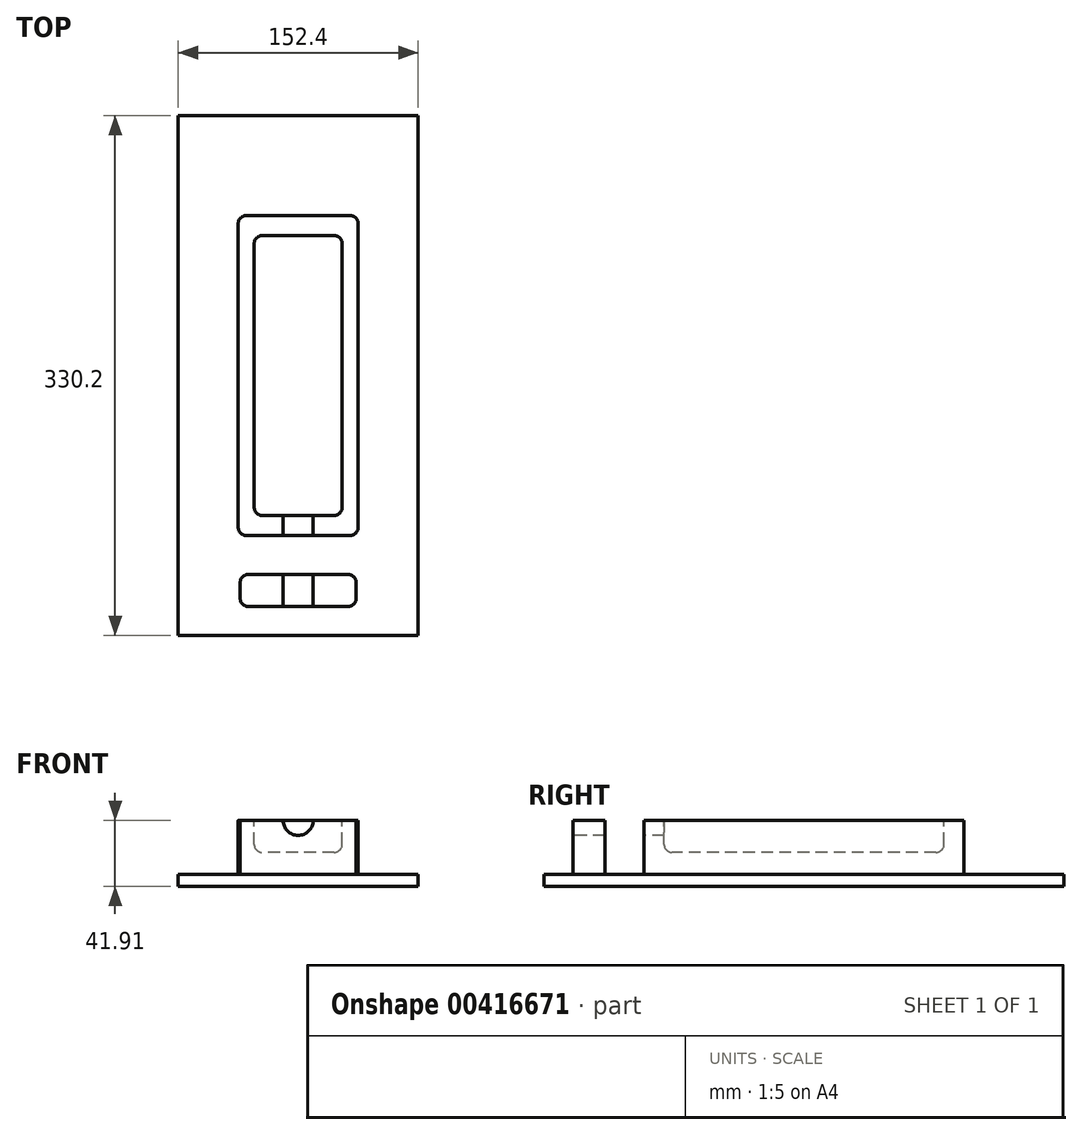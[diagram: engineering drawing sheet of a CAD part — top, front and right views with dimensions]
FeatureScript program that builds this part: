
annotation { "Feature Type Name" : "Feature", "Feature Type Description" : "" }
export const myFeature = defineFeature(function(context is Context, id is Id, definition is map)
    precondition{}
    {
        {
            var Q0;
            Q0=qCreatedBy(makeId("Top.planeOp"),FACE);
            var sketch = newSketch(context, id + "F0", { "sketchPlane" : qUnion([Q0])});
            skLineSegment(sketch, "E0.bottom", {"start": v(38.1, 101.6) * mm, "end": v(-38.1, 101.6) * mm});
            skLineSegment(sketch, "E0.top", {"start": v(38.1, -101.6) * mm, "end": v(-38.1, -101.6) * mm});
            skLineSegment(sketch, "E0.left", {"start": v(38.1, 101.6) * mm, "end": v(38.1, -101.6) * mm});
            skLineSegment(sketch, "E0.right", {"start": v(-38.1, 101.6) * mm, "end": v(-38.1, -101.6) * mm});
            skPoint(sketch, "E0.middle", {"position": v(0, 0) * mm});
            skSolve(sketch);
        }
        {
            var Q0;
            Q0=makeQuery(id+"F0.imprint","IMPRINT",FACE,{"disambiguationData":[TD([[makeQuery(id+"F0.imprint","IMPRINT",EDGE,{"derivedFrom":sQuery(id+"F0.wireOp",EDGE,"E0.bottom")}),1.0]])]});
            extrude(context, id + "F1", {"entities" : qUnion([Q0]), "endBound" : BoundingType.SYMMETRIC, "depth" : 38.1 * mm});
        }
        {
            var Q0;
            Q0=makeQuery(id+"F1.opExtrude","CAP_FACE",FACE,{"disambiguationData":[OSD([sQuery(id+"F0.wireOp",EDGE,"E0.bottom"),sQuery(id+"F0.wireOp",EDGE,"E0.top"),sQuery(id+"F0.wireOp",EDGE,"E0.left"),sQuery(id+"F0.wireOp",EDGE,"E0.right")])],"isStart":false});
            var sketch = newSketch(context, id + "F2", { "sketchPlane" : qUnion([Q0])});
            skLineSegment(sketch, "E1.bottom", {"start": v(27.94, 88.9) * mm, "end": v(-27.94, 88.9) * mm});
            skLineSegment(sketch, "E1.top", {"start": v(27.94, -88.9) * mm, "end": v(-27.94, -88.9) * mm});
            skLineSegment(sketch, "E1.left", {"start": v(27.94, 88.9) * mm, "end": v(27.94, -88.9) * mm});
            skLineSegment(sketch, "E1.right", {"start": v(-27.94, 88.9) * mm, "end": v(-27.94, -88.9) * mm});
            skPoint(sketch, "E1.middle", {"position": v(0, 0) * mm});
            skSolve(sketch);
        }
        {
            var Q0;
            Q0=makeQuery(id+"F2.imprint","IMPRINT",FACE,{"disambiguationData":[TD([[makeQuery(id+"F2.imprint","IMPRINT",EDGE,{"derivedFrom":sQuery(id+"F2.wireOp",EDGE,"E1.bottom")}),1.0]])]});
            extrude(context, id + "F3", {"entities" : qUnion([Q0]), "operationType" : NewBodyOperationType.REMOVE, "oppositeDirection" : true, "depth" : 20.32 * mm});
        }
        {
            var Q0;
            Q0=makeQuery(id+"F3.boolean.opBoolean","COPY",EDGE,{"derivedFrom":makeQuery(id+"F3.opExtrude","CAP_EDGE",EDGE,{"disambiguationData":[OSD([sQuery(id+"F2.wireOp",EDGE,"E1.right")])],"isStart":false})});
            var Q1;
            Q1=makeQuery(id+"F3.boolean.opBoolean","COPY",EDGE,{"derivedFrom":makeQuery(id+"F3.opExtrude","CAP_EDGE",EDGE,{"disambiguationData":[OSD([sQuery(id+"F2.wireOp",EDGE,"E1.bottom")])],"isStart":false})});
            var Q2;
            Q2=makeQuery(id+"F3.boolean.opBoolean","COPY",EDGE,{"derivedFrom":makeQuery(id+"F3.opExtrude","CAP_EDGE",EDGE,{"disambiguationData":[OSD([sQuery(id+"F2.wireOp",EDGE,"E1.left")])],"isStart":false})});
            var Q3;
            Q3=makeQuery(id+"F3.boolean.opBoolean","COPY",EDGE,{"derivedFrom":makeQuery(id+"F3.opExtrude","CAP_EDGE",EDGE,{"disambiguationData":[OSD([sQuery(id+"F2.wireOp",EDGE,"E1.top")])],"isStart":false})});
            var Q4;
            Q4=makeQuery(id+"F3.boolean.opBoolean","COPY",EDGE,{"derivedFrom":makeQuery(id+"F3.opExtrude","SWEPT_EDGE",EDGE,{"disambiguationData":[OSD([sQuery(id+"F2.wireOp",EDGE,"E1.bottom"),sQuery(id+"F2.wireOp",EDGE,"E1.right")])]})});
            var Q5;
            Q5=makeQuery(id+"F3.boolean.opBoolean","COPY",EDGE,{"derivedFrom":makeQuery(id+"F3.opExtrude","SWEPT_EDGE",EDGE,{"disambiguationData":[OSD([sQuery(id+"F2.wireOp",EDGE,"E1.bottom"),sQuery(id+"F2.wireOp",EDGE,"E1.left")])]})});
            var Q6;
            Q6=makeQuery(id+"F3.boolean.opBoolean","COPY",EDGE,{"derivedFrom":makeQuery(id+"F3.opExtrude","SWEPT_EDGE",EDGE,{"disambiguationData":[OSD([sQuery(id+"F2.wireOp",EDGE,"E1.top"),sQuery(id+"F2.wireOp",EDGE,"E1.left")])]})});
            var Q7;
            Q7=makeQuery(id+"F3.boolean.opBoolean","COPY",EDGE,{"derivedFrom":makeQuery(id+"F3.opExtrude","SWEPT_EDGE",EDGE,{"disambiguationData":[OSD([sQuery(id+"F2.wireOp",EDGE,"E1.top"),sQuery(id+"F2.wireOp",EDGE,"E1.right")])]})});
            var Q8;
            Q8=makeQuery(id+"F3.boolean.opBoolean","COPY",EDGE,{"derivedFrom":makeQuery(id+"F3.opExtrude","CAP_EDGE",EDGE,{"disambiguationData":[OSD([sQuery(id+"F2.wireOp",EDGE,"E1.bottom")])],"isStart":true})});
            fillet(context, id + "F4", {"entities" : qUnion([Q0, Q1, Q2, Q3, Q4, Q5, Q6, Q7, Q8]), "radius" : 5.08 * mm, "tangentPropagation" : true, "allowEdgeOverflow" : false});
        }
        {
            var Q0;
            Q0=makeQuery(id+"F1.opExtrude","SWEPT_FACE",FACE,{"disambiguationData":[OSD([sQuery(id+"F0.wireOp",EDGE,"E0.top")])]});
            var sketch = newSketch(context, id + "F5", { "sketchPlane" : qUnion([Q0])});
            skArc(sketch, "E2", {"start": v(-9.53, 19.05) * mm, "mid": v(0, 9.53) * mm, "end": v(9.52, 19.05) * mm});
            skSolve(sketch);
        }
        {
            var Q0;
            {var subQ0=sQuery(id+"F5.wireOp",EDGE,"E2");Q0=makeQuery(id+"F5.imprint","IMPRINT",FACE,{"disambiguationData":[TD([[makeQuery(id+"F5.imprint","IMPRINT",EDGE,{"derivedFrom":subQ0}),1.0]])]});}
            extrude(context, id + "F6", {"entities" : qUnion([Q0]), "operationType" : NewBodyOperationType.REMOVE, "oppositeDirection" : true, "depth" : 25.4 * mm});
        }
        {
            var Q0;
            Q0=makeQuery(id+"F1.opExtrude","CAP_FACE",FACE,{"disambiguationData":[OSD([sQuery(id+"F0.wireOp",EDGE,"E0.bottom"),sQuery(id+"F0.wireOp",EDGE,"E0.top"),sQuery(id+"F0.wireOp",EDGE,"E0.left"),sQuery(id+"F0.wireOp",EDGE,"E0.right")])],"isStart":true});
            var sketch = newSketch(context, id + "F7", { "sketchPlane" : qUnion([Q0])});
            skLineSegment(sketch, "E3.bottom", {"start": v(76.2, 165.1) * mm, "end": v(-76.2, 165.1) * mm});
            skLineSegment(sketch, "E3.top", {"start": v(76.2, -165.1) * mm, "end": v(-76.2, -165.1) * mm});
            skLineSegment(sketch, "E3.left", {"start": v(76.2, 165.1) * mm, "end": v(76.2, -165.1) * mm});
            skLineSegment(sketch, "E3.right", {"start": v(-76.2, 165.1) * mm, "end": v(-76.2, -165.1) * mm});
            skPoint(sketch, "E3.middle", {"position": v(0, 0) * mm});
            skSolve(sketch);
        }
        {
            var Q0;
            Q0=makeQuery(id+"F7.imprint","IMPRINT",FACE,{"disambiguationData":[TD([[makeQuery(id+"F7.imprint","IMPRINT",EDGE,{"derivedFrom":sQuery(id+"F7.wireOp",EDGE,"E3.bottom")}),1.0]])]});
            var Q1;
            Q1=makeQuery(id+"F7.imprint","IMPRINT",FACE,{"disambiguationData":[TD([[makeQuery(id+"F7.imprint","IMPRINT",EDGE,{"derivedFrom":makeQuery(id+"F1.opExtrude","CAP_EDGE",EDGE,{"disambiguationData":[OSD([sQuery(id+"F0.wireOp",EDGE,"E0.bottom")])],"isStart":true})}),-1.0]])]});
            extrude(context, id + "F8", {"entities" : qUnion([Q0, Q1]), "operationType" : NewBodyOperationType.ADD, "endBound" : BoundingType.SYMMETRIC, "depth" : 7.62 * mm});
        }
        {
            var Q0;
            Q0=makeQuery(id+"F8.opExtrude","CAP_FACE",FACE,{"disambiguationData":[OSD([sQuery(id+"F0.wireOp",EDGE,"E0.bottom"),sQuery(id+"F0.wireOp",EDGE,"E0.top"),sQuery(id+"F0.wireOp",EDGE,"E0.left"),sQuery(id+"F0.wireOp",EDGE,"E0.right"),sQuery(id+"F7.wireOp",EDGE,"E3.bottom"),sQuery(id+"F7.wireOp",EDGE,"E3.top"),sQuery(id+"F7.wireOp",EDGE,"E3.left"),sQuery(id+"F7.wireOp",EDGE,"E3.right")])],"isStart":true});
            var sketch = newSketch(context, id + "F9", { "sketchPlane" : qUnion([Q0])});
            skLineSegment(sketch, "E4.bottom", {"start": v(36.83, -126.41) * mm, "end": v(-36.83, -126.41) * mm});
            skLineSegment(sketch, "E4.top", {"start": v(36.83, -146.73) * mm, "end": v(-36.83, -146.73) * mm});
            skLineSegment(sketch, "E4.left", {"start": v(36.83, -126.41) * mm, "end": v(36.83, -146.73) * mm});
            skLineSegment(sketch, "E4.right", {"start": v(-36.83, -126.41) * mm, "end": v(-36.83, -146.73) * mm});
            skPoint(sketch, "E4.middle", {"position": v(0, -136.57) * mm});
            skSolve(sketch);
        }
        {
            var Q0;
            Q0=makeQuery(id+"F9.imprint","IMPRINT",FACE,{"disambiguationData":[TD([[makeQuery(id+"F9.imprint","IMPRINT",EDGE,{"derivedFrom":sQuery(id+"F9.wireOp",EDGE,"E4.bottom")}),1.0]])]});
            extrude(context, id + "F10", {"entities" : qUnion([Q0]), "operationType" : NewBodyOperationType.ADD, "depth" : 34.3 * mm});
        }
        {
            var Q0;
            Q0=makeQuery(id+"F10.opExtrude","SWEPT_FACE",FACE,{"disambiguationData":[OSD([sQuery(id+"F9.wireOp",EDGE,"E4.top")])]});
            var sketch = newSketch(context, id + "F11", { "sketchPlane" : qUnion([Q0])});
            skArc(sketch, "E5", {"start": v(-9.52, 19.05) * mm, "mid": v(0, 9.53) * mm, "end": v(9.53, 19.05) * mm});
            skSolve(sketch);
        }
        {
            var Q0;
            {var subQ0=sQuery(id+"F11.wireOp",EDGE,"E5");Q0=makeQuery(id+"F11.imprint","IMPRINT",FACE,{"disambiguationData":[TD([[makeQuery(id+"F11.imprint","IMPRINT",EDGE,{"derivedFrom":subQ0}),1.0]])]});}
            extrude(context, id + "F12", {"entities" : qUnion([Q0]), "operationType" : NewBodyOperationType.REMOVE, "oppositeDirection" : true, "depth" : 25.4 * mm});
        }
        {
            var Q0;
            Q0=makeQuery(id+"F1.opExtrude","SWEPT_EDGE",EDGE,{"disambiguationData":[OSD([sQuery(id+"F0.wireOp",EDGE,"E0.top"),sQuery(id+"F0.wireOp",EDGE,"E0.left")])]});
            var Q1;
            Q1=makeQuery(id+"F10.opExtrude","SWEPT_EDGE",EDGE,{"disambiguationData":[OSD([sQuery(id+"F9.wireOp",EDGE,"E4.bottom"),sQuery(id+"F9.wireOp",EDGE,"E4.left")])]});
            var Q2;
            Q2=makeQuery(id+"F10.opExtrude","SWEPT_EDGE",EDGE,{"disambiguationData":[OSD([sQuery(id+"F9.wireOp",EDGE,"E4.top"),sQuery(id+"F9.wireOp",EDGE,"E4.left")])]});
            var Q3;
            Q3=makeQuery(id+"F10.opExtrude","SWEPT_EDGE",EDGE,{"disambiguationData":[OSD([sQuery(id+"F9.wireOp",EDGE,"E4.top"),sQuery(id+"F9.wireOp",EDGE,"E4.right")])]});
            var Q4;
            Q4=makeQuery(id+"F10.opExtrude","SWEPT_EDGE",EDGE,{"disambiguationData":[OSD([sQuery(id+"F9.wireOp",EDGE,"E4.bottom"),sQuery(id+"F9.wireOp",EDGE,"E4.right")])]});
            var Q5;
            Q5=makeQuery(id+"F1.opExtrude","SWEPT_EDGE",EDGE,{"disambiguationData":[OSD([sQuery(id+"F0.wireOp",EDGE,"E0.top"),sQuery(id+"F0.wireOp",EDGE,"E0.right")])]});
            var Q6;
            Q6=makeQuery(id+"F1.opExtrude","SWEPT_EDGE",EDGE,{"disambiguationData":[OSD([sQuery(id+"F0.wireOp",EDGE,"E0.bottom"),sQuery(id+"F0.wireOp",EDGE,"E0.left")])]});
            var Q7;
            Q7=makeQuery(id+"F1.opExtrude","SWEPT_EDGE",EDGE,{"disambiguationData":[OSD([sQuery(id+"F0.wireOp",EDGE,"E0.bottom"),sQuery(id+"F0.wireOp",EDGE,"E0.right")])]});
            fillet(context, id + "F13", {"entities" : qUnion([Q0, Q1, Q2, Q3, Q4, Q5, Q6, Q7]), "radius" : 5.08 * mm, "tangentPropagation" : true, "allowEdgeOverflow" : false});
        }
    });
